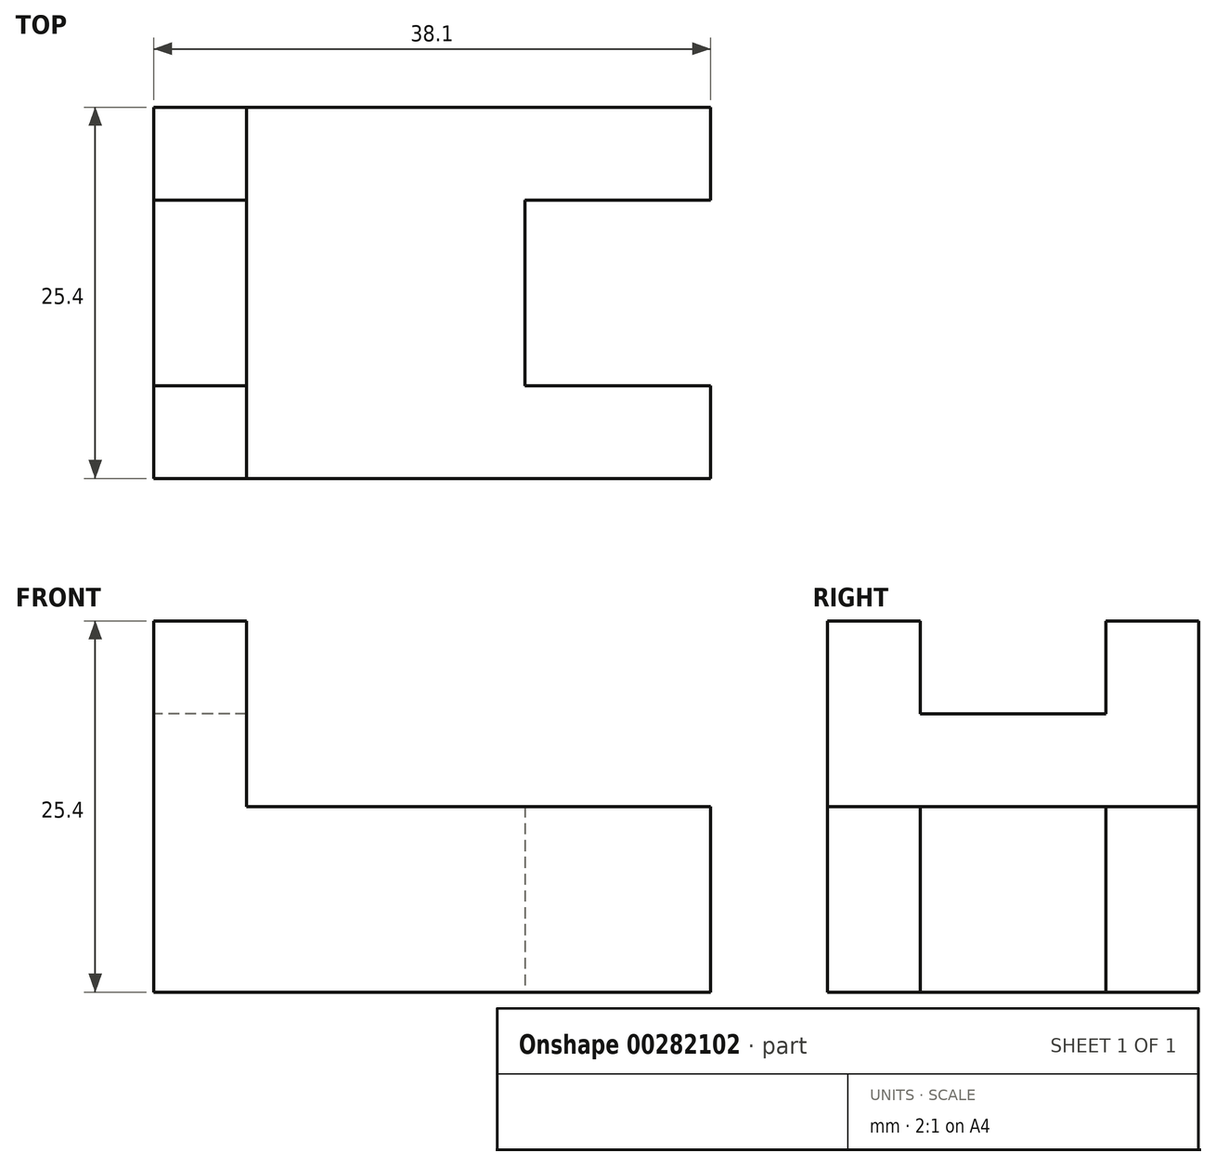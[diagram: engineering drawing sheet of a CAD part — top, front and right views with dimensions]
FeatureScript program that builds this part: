
annotation { "Feature Type Name" : "Feature", "Feature Type Description" : "" }
export const myFeature = defineFeature(function(context is Context, id is Id, definition is map)
    precondition{}
    {
        {
            var Q0;
            Q0=qCreatedBy(makeId("Top.planeOp"),FACE);
            var sketch = newSketch(context, id + "F0", { "sketchPlane" : qUnion([Q0])});
            skLineSegment(sketch, "E0", {"start": v(0, 12.7) * mm, "end": v(0, -12.7) * mm});
            skLineSegment(sketch, "E1", {"start": v(0, 12.7) * mm, "end": v(38.1, 12.7) * mm});
            skLineSegment(sketch, "E2", {"start": v(38.1, 12.7) * mm, "end": v(38.1, 6.35) * mm});
            skLineSegment(sketch, "E3", {"start": v(38.1, 6.35) * mm, "end": v(25.4, 6.35) * mm});
            skLineSegment(sketch, "E4", {"start": v(25.4, 6.35) * mm, "end": v(25.4, -6.35) * mm});
            skLineSegment(sketch, "E5", {"start": v(25.4, -6.35) * mm, "end": v(38.1, -6.35) * mm});
            skLineSegment(sketch, "E6", {"start": v(38.1, -6.35) * mm, "end": v(38.1, -12.7) * mm});
            skLineSegment(sketch, "E7", {"start": v(38.1, -12.7) * mm, "end": v(0, -12.7) * mm});
            skLineSegment(sketch, "E8", {"start": v(-24.07, 0) * mm, "end": v(60.47, 0) * mm, "construction": true});
            skSolve(sketch);
        }
        {
            var Q0;
            Q0 = qSketchRegion(id + "F0", true);
            extrude(context, id + "F1", {"entities" : qUnion([Q0]), "depth" : 12.7 * mm});
        }
        {
            var Q0;
            Q0=qCreatedBy(makeId("Right.planeOp"),FACE);
            var sketch = newSketch(context, id + "F2", { "sketchPlane" : qUnion([Q0])});
            skLineSegment(sketch, "E9", {"start": v(-12.7, 12.7) * mm, "end": v(-12.7, 25.4) * mm});
            skLineSegment(sketch, "E10", {"start": v(-12.7, 25.4) * mm, "end": v(-6.35, 25.4) * mm});
            skLineSegment(sketch, "E11", {"start": v(-6.35, 25.4) * mm, "end": v(-6.35, 19.05) * mm});
            skLineSegment(sketch, "E12", {"start": v(-6.35, 19.05) * mm, "end": v(6.35, 19.05) * mm});
            skLineSegment(sketch, "E13", {"start": v(6.35, 19.05) * mm, "end": v(6.35, 25.4) * mm});
            skLineSegment(sketch, "E14", {"start": v(6.35, 25.4) * mm, "end": v(12.7, 25.4) * mm});
            skLineSegment(sketch, "E15", {"start": v(12.7, 25.4) * mm, "end": v(12.7, 12.7) * mm});
            skLineSegment(sketch, "E16", {"start": v(-12.7, 12.7) * mm, "end": v(12.7, 12.7) * mm});
            skSolve(sketch);
        }
        {
            var Q0;
            Q0 = qSketchRegion(id + "F2", true);
            extrude(context, id + "F3", {"entities" : qUnion([Q0]), "operationType" : NewBodyOperationType.ADD, "depth" : 6.35 * mm});
        }
    });
